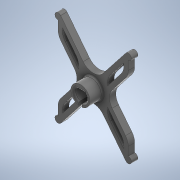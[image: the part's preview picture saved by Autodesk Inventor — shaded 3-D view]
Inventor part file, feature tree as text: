
AUTODESK INVENTOR PART (.ipt)
format: ipt  version: 2020 (Build 240168000, 168)  size: 359,424 bytes
history: native  units: in
note: dims shown in document units (in); Inventor stores cm internally (conversion verified against a paired STEP export)
features: extrude x2, fillet x2, sketch x1
ambient origin geometry x8: Origin, YZ Plane, XZ Plane, XY Plane, X Axis, Y Axis, Z Axis, Center Point
bodies: Solid1 (feature_tree)
feature tree (5):
  extrude  "Extrusion1"  Depth=0.0312in
  fillet  "Fillet1"  Radius=0.125in
  extrude  "Extrusion2"  Depth=0.0312in
  fillet  "Fillet2"  Radius=0.125in
  sketch  "Sketch2"  dims[d0=1.375in d1=1.75in d2=0.125in d4=0.5in d7=0.125in d8=0.0in d9=0.25in d10=0.25in d11=0.375in d13=0.25in d14=0.0in d15=0.0312in d22=0.216in d23=0.0625in d24=0.5in d25=0.0344in]
